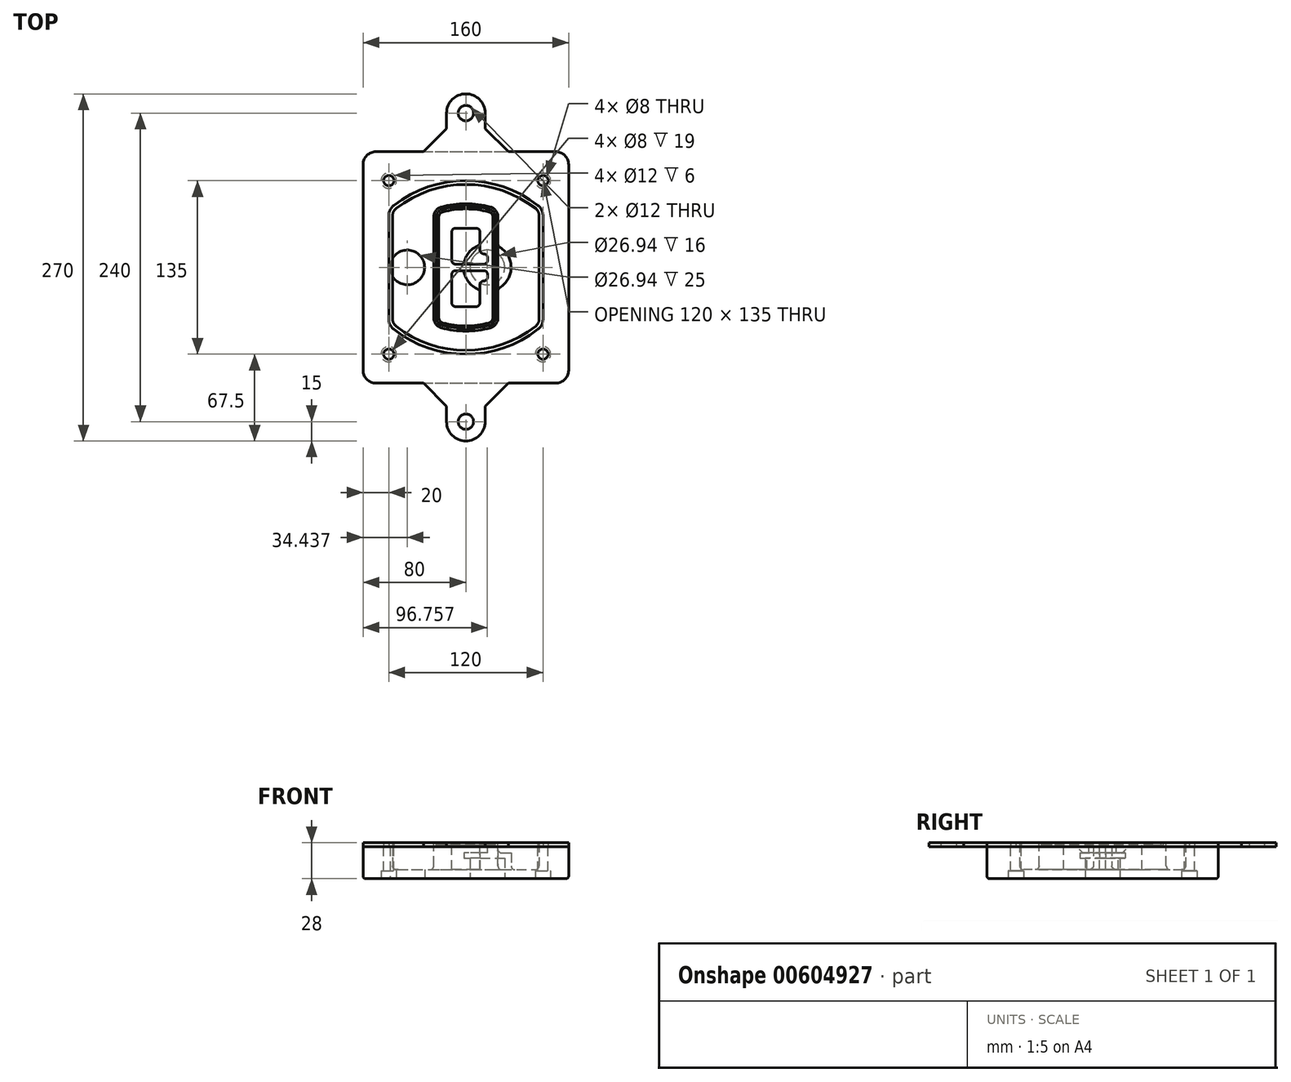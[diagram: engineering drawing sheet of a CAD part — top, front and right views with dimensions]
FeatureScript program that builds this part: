
annotation { "Feature Type Name" : "Feature", "Feature Type Description" : "" }
export const myFeature = defineFeature(function(context is Context, id is Id, definition is map)
    precondition{}
    {
        {
            var Q0;
            Q0=qCreatedBy(makeId("Top.planeOp"),FACE);
            var sketch = newSketch(context, id + "F0", { "sketchPlane" : qUnion([Q0])});
            skPoint(sketch, "E0.rect.middle", {"position": v(0, 0) * mm});
            skLineSegment(sketch, "E1.bottom", {"start": v(-70, -90) * mm, "end": v(70, -90) * mm});
            skLineSegment(sketch, "E1.top", {"start": v(-70, 90) * mm, "end": v(70, 90) * mm});
            skLineSegment(sketch, "E1.left", {"start": v(-80, -80) * mm, "end": v(-80, 80) * mm});
            skLineSegment(sketch, "E1.right", {"start": v(80, -80) * mm, "end": v(80, 80) * mm});
            skLineSegment(sketch, "E2", {"start": v(-80, 90) * mm, "end": v(80, -90) * mm, "construction": true});
            skLineSegment(sketch, "E3", {"start": v(80, 90) * mm, "end": v(-80, -90) * mm, "construction": true});
            skCircle(sketch, "E4", {"center": v(-60, 67.5) * mm, "radius": 4 * mm});
            skCircle(sketch, "E5", {"center": v(60, 67.5) * mm, "radius": 4 * mm});
            skCircle(sketch, "E6", {"center": v(60, -67.5) * mm, "radius": 4 * mm});
            skCircle(sketch, "E7", {"center": v(-60, -67.5) * mm, "radius": 4 * mm});
            skLineSegment(sketch, "E8", {"start": v(-60, 67.5) * mm, "end": v(60, 67.5) * mm, "construction": true});
            skLineSegment(sketch, "E9", {"start": v(60, 67.5) * mm, "end": v(60, -67.5) * mm, "construction": true});
            skLineSegment(sketch, "E10", {"start": v(60, -67.5) * mm, "end": v(-60, -67.5) * mm, "construction": true});
            skLineSegment(sketch, "E11", {"start": v(-60, -67.5) * mm, "end": v(-60, 67.5) * mm, "construction": true});
            skLineSegment(sketch, "E12", {"start": v(-60, 40.3) * mm, "end": v(-60, -40.3) * mm});
            skLineSegment(sketch, "E13", {"start": v(60, 40.3) * mm, "end": v(60, -40.3) * mm});
            skArc(sketch, "E14", {"start": v(56.15, 48.18) * mm, "mid": v(0, 67.5) * mm, "end": v(-56.15, 48.18) * mm});
            skArc(sketch, "E15", {"start": v(-56.15, -48.18) * mm, "mid": v(0, -67.5) * mm, "end": v(56.15, -48.18) * mm});
            skLineSegment(sketch, "E16", {"start": v(-60, 0) * mm, "end": v(60, 0) * mm, "construction": true});
            skPoint(sketch, "E17.visualSharp", {"position": v(-60, -45) * mm});
            skArc(sketch, "E17.filletArc", {"start": v(-60, -40.3) * mm, "mid": v(-58.99, -44.68) * mm, "end": v(-56.15, -48.18) * mm});
            skPoint(sketch, "E18.visualSharp", {"position": v(-60, 45) * mm});
            skArc(sketch, "E18.filletArc", {"start": v(-56.15, 48.18) * mm, "mid": v(-58.99, 44.68) * mm, "end": v(-60, 40.3) * mm});
            skPoint(sketch, "E19.visualSharp", {"position": v(60, 45) * mm});
            skArc(sketch, "E19.filletArc", {"start": v(60, 40.3) * mm, "mid": v(58.99, 44.68) * mm, "end": v(56.15, 48.18) * mm});
            skPoint(sketch, "E20.visualSharp", {"position": v(60, -45) * mm});
            skArc(sketch, "E20.filletArc", {"start": v(56.15, -48.18) * mm, "mid": v(58.99, -44.68) * mm, "end": v(60, -40.3) * mm});
            skPoint(sketch, "E21.visualSharp", {"position": v(-80, 90) * mm});
            skArc(sketch, "E21.filletArc", {"start": v(-70, 90) * mm, "mid": v(-77.07, 87.07) * mm, "end": v(-80, 80) * mm});
            skPoint(sketch, "E22.visualSharp", {"position": v(80, 90) * mm});
            skArc(sketch, "E22.filletArc", {"start": v(80, 80) * mm, "mid": v(77.07, 87.07) * mm, "end": v(70, 90) * mm});
            skPoint(sketch, "E23.visualSharp", {"position": v(80, -90) * mm});
            skArc(sketch, "E23.filletArc", {"start": v(70, -90) * mm, "mid": v(77.07, -87.07) * mm, "end": v(80, -80) * mm});
            skPoint(sketch, "E24.visualSharp", {"position": v(-80, -90) * mm});
            skArc(sketch, "E24.filletArc", {"start": v(-80, -80) * mm, "mid": v(-77.07, -87.07) * mm, "end": v(-70, -90) * mm});
            skArc(sketch, "E25.0", {"start": v(57, 40.3) * mm, "mid": v(56.3, 43.36) * mm, "end": v(54.3, 45.81) * mm});
            skLineSegment(sketch, "E25.1", {"start": v(57, 40.3) * mm, "end": v(57, -40.3) * mm});
            skArc(sketch, "E25.2", {"start": v(54.3, -45.81) * mm, "mid": v(56.3, -43.36) * mm, "end": v(57, -40.3) * mm});
            skArc(sketch, "E25.3", {"start": v(-54.3, -45.81) * mm, "mid": v(0, -64.5) * mm, "end": v(54.3, -45.81) * mm});
            skArc(sketch, "E25.4", {"start": v(-57, -40.3) * mm, "mid": v(-56.3, -43.36) * mm, "end": v(-54.3, -45.81) * mm});
            skArc(sketch, "E25.5", {"start": v(54.3, 45.81) * mm, "mid": v(0, 64.5) * mm, "end": v(-54.3, 45.81) * mm});
            skLineSegment(sketch, "E25.6", {"start": v(-57, 40.3) * mm, "end": v(-57, -40.3) * mm});
            skArc(sketch, "E25.7", {"start": v(-54.3, 45.81) * mm, "mid": v(-56.3, 43.36) * mm, "end": v(-57, 40.3) * mm});
            skArc(sketch, "E26.0", {"start": v(-58.62, 51.33) * mm, "mid": v(-62.58, 46.43) * mm, "end": v(-64, 40.3) * mm});
            skArc(sketch, "E26.1", {"start": v(58.62, 51.33) * mm, "mid": v(0, 71.5) * mm, "end": v(-58.62, 51.33) * mm});
            skArc(sketch, "E26.2", {"start": v(64, 40.3) * mm, "mid": v(62.58, 46.43) * mm, "end": v(58.62, 51.33) * mm});
            skLineSegment(sketch, "E26.3", {"start": v(64, 40.3) * mm, "end": v(64, -40.3) * mm});
            skArc(sketch, "E26.4", {"start": v(58.62, -51.33) * mm, "mid": v(62.58, -46.43) * mm, "end": v(64, -40.3) * mm});
            skLineSegment(sketch, "E26.5", {"start": v(-64, 40.3) * mm, "end": v(-64, -40.3) * mm});
            skArc(sketch, "E26.6", {"start": v(-58.62, -51.33) * mm, "mid": v(0, -71.5) * mm, "end": v(58.62, -51.33) * mm});
            skArc(sketch, "E26.7", {"start": v(-64, -40.3) * mm, "mid": v(-62.58, -46.43) * mm, "end": v(-58.62, -51.33) * mm});
            skSolve(sketch);
        }
        {
            var Q0;
            Q0=makeQuery(id+"F0.imprint","IMPRINT",FACE,{"disambiguationData":[TD([[makeQuery(id+"F0.imprint","IMPRINT",EDGE,{"derivedFrom":sQuery(id+"F0.wireOp",EDGE,"E1.bottom")}),1.0]])]});
            var Q1;
            Q1=makeQuery(id+"F0.imprint","IMPRINT",FACE,{"disambiguationData":[TD([[makeQuery(id+"F0.imprint","IMPRINT",EDGE,{"derivedFrom":sQuery(id+"F0.wireOp",EDGE,"E12")}),1.0]])]});
            var Q2;
            Q2=makeQuery(id+"F0.imprint","IMPRINT",FACE,{"disambiguationData":[TD([[makeQuery(id+"F0.imprint","IMPRINT",EDGE,{"derivedFrom":sQuery(id+"F0.wireOp",EDGE,"E25.0")}),1.0]])]});
            var Q3;
            Q3=makeQuery(id+"F0.imprint","IMPRINT",FACE,{"disambiguationData":[TD([[makeQuery(id+"F0.imprint","IMPRINT",EDGE,{"derivedFrom":sQuery(id+"F0.wireOp",EDGE,"E12")}),-1.0]])]});
            extrude(context, id + "F1", {"entities" : qUnion([Q0, Q1, Q2, Q3]), "oppositeDirection" : true, "depth" : 25 * mm});
        }
        {
            var Q0;
            Q0=makeQuery(id+"F0.imprint","IMPRINT",FACE,{"disambiguationData":[TD([[makeQuery(id+"F0.imprint","IMPRINT",EDGE,{"derivedFrom":sQuery(id+"F0.wireOp",EDGE,"E12")}),1.0]])]});
            extrude(context, id + "F2", {"entities" : qUnion([Q0]), "operationType" : NewBodyOperationType.ADD, "depth" : 3 * mm});
        }
        {
            var Q0;
            Q0=makeQuery(id+"F0.imprint","IMPRINT",FACE,{"disambiguationData":[TD([[makeQuery(id+"F0.imprint","IMPRINT",EDGE,{"derivedFrom":sQuery(id+"F0.wireOp",EDGE,"E25.0")}),1.0]])]});
            extrude(context, id + "F3", {"entities" : qUnion([Q0]), "operationType" : NewBodyOperationType.REMOVE, "oppositeDirection" : true, "depth" : 18 * mm});
        }
        {
            var Q0;
            Q0=makeQuery(id+"F2.opExtrude","CAP_FACE",FACE,{"disambiguationData":[OSD([sQuery(id+"F0.wireOp",EDGE,"E12"),sQuery(id+"F0.wireOp",EDGE,"E13"),sQuery(id+"F0.wireOp",EDGE,"E14"),sQuery(id+"F0.wireOp",EDGE,"E15"),sQuery(id+"F0.wireOp",EDGE,"E17.filletArc"),sQuery(id+"F0.wireOp",EDGE,"E18.filletArc"),sQuery(id+"F0.wireOp",EDGE,"E19.filletArc"),sQuery(id+"F0.wireOp",EDGE,"E20.filletArc"),sQuery(id+"F0.wireOp",EDGE,"E25.0"),sQuery(id+"F0.wireOp",EDGE,"E25.1"),sQuery(id+"F0.wireOp",EDGE,"E25.2"),sQuery(id+"F0.wireOp",EDGE,"E25.3"),sQuery(id+"F0.wireOp",EDGE,"E25.4"),sQuery(id+"F0.wireOp",EDGE,"E25.5"),sQuery(id+"F0.wireOp",EDGE,"E25.6"),sQuery(id+"F0.wireOp",EDGE,"E25.7")])],"isStart":false});
            var sketch = newSketch(context, id + "F4", { "sketchPlane" : qUnion([Q0])});
            skArc(sketch, "E27.0", {"start": v(-19.08, -46.97) * mm, "mid": v(0, -49.5) * mm, "end": v(19.08, -46.97) * mm});
            skArc(sketch, "E28.0", {"start": v(19.08, 46.97) * mm, "mid": v(0, 49.5) * mm, "end": v(-19.08, 46.97) * mm});
            skLineSegment(sketch, "E29", {"start": v(-25, 39.25) * mm, "end": v(-25, -39.25) * mm});
            skLineSegment(sketch, "E30", {"start": v(25, 39.25) * mm, "end": v(25, -39.25) * mm});
            skLineSegment(sketch, "E31", {"start": v(-25, 45.1) * mm, "end": v(25, 45.1) * mm, "construction": true});
            skLineSegment(sketch, "E32", {"start": v(-25, -45.1) * mm, "end": v(25, -45.1) * mm, "construction": true});
            skPoint(sketch, "E33.visualSharp", {"position": v(-25, 45.1) * mm});
            skArc(sketch, "E33.filletArc", {"start": v(-19.08, 46.97) * mm, "mid": v(-23.35, 44.11) * mm, "end": v(-25, 39.25) * mm});
            skPoint(sketch, "E34.visualSharp", {"position": v(25, 45.1) * mm});
            skArc(sketch, "E34.filletArc", {"start": v(25, 39.25) * mm, "mid": v(23.35, 44.11) * mm, "end": v(19.08, 46.97) * mm});
            skPoint(sketch, "E35.visualSharp", {"position": v(25, -45.1) * mm});
            skArc(sketch, "E35.filletArc", {"start": v(19.08, -46.97) * mm, "mid": v(23.35, -44.11) * mm, "end": v(25, -39.25) * mm});
            skPoint(sketch, "E36.visualSharp", {"position": v(-25, -45.1) * mm});
            skArc(sketch, "E36.filletArc", {"start": v(-25, -39.25) * mm, "mid": v(-23.35, -44.11) * mm, "end": v(-19.08, -46.97) * mm});
            skArc(sketch, "E37.0", {"start": v(54.3, 45.81) * mm, "mid": v(0, 64.5) * mm, "end": v(-54.3, 45.81) * mm});
            skArc(sketch, "E37.1", {"start": v(-54.3, 45.81) * mm, "mid": v(-56.3, 43.36) * mm, "end": v(-57, 40.3) * mm});
            skLineSegment(sketch, "E37.2", {"start": v(-57, 40.3) * mm, "end": v(-57, -40.3) * mm});
            skArc(sketch, "E37.3", {"start": v(-57, -40.3) * mm, "mid": v(-56.3, -43.36) * mm, "end": v(-54.3, -45.81) * mm});
            skArc(sketch, "E37.4", {"start": v(-54.3, -45.81) * mm, "mid": v(0, -64.5) * mm, "end": v(54.3, -45.81) * mm});
            skArc(sketch, "E37.5", {"start": v(54.3, -45.81) * mm, "mid": v(56.3, -43.36) * mm, "end": v(57, -40.3) * mm});
            skLineSegment(sketch, "E37.6", {"start": v(57, 40.3) * mm, "end": v(57, -40.3) * mm});
            skArc(sketch, "E37.7", {"start": v(57, 40.3) * mm, "mid": v(56.3, 43.36) * mm, "end": v(54.3, 45.81) * mm});
            skLineSegment(sketch, "E38.0", {"start": v(23, 39.25) * mm, "end": v(23, -39.25) * mm});
            skArc(sketch, "E38.1", {"start": v(18.56, -45.04) * mm, "mid": v(21.76, -42.9) * mm, "end": v(23, -39.25) * mm});
            skArc(sketch, "E38.2", {"start": v(-18.56, -45.04) * mm, "mid": v(0, -47.5) * mm, "end": v(18.56, -45.04) * mm});
            skArc(sketch, "E38.3", {"start": v(-23, -39.25) * mm, "mid": v(-21.76, -42.9) * mm, "end": v(-18.56, -45.04) * mm});
            skLineSegment(sketch, "E38.4", {"start": v(-23, 39.25) * mm, "end": v(-23, -39.25) * mm});
            skArc(sketch, "E38.5", {"start": v(23, 39.25) * mm, "mid": v(21.76, 42.9) * mm, "end": v(18.56, 45.04) * mm});
            skArc(sketch, "E38.6", {"start": v(-18.56, 45.04) * mm, "mid": v(-21.76, 42.9) * mm, "end": v(-23, 39.25) * mm});
            skArc(sketch, "E38.7", {"start": v(18.56, 45.04) * mm, "mid": v(0, 47.5) * mm, "end": v(-18.56, 45.04) * mm});
            skArc(sketch, "E39.0", {"start": v(21, 39.25) * mm, "mid": v(20.18, 41.68) * mm, "end": v(18.04, 43.1) * mm});
            skLineSegment(sketch, "E39.1", {"start": v(21, 39.25) * mm, "end": v(21, -39.25) * mm});
            skArc(sketch, "E39.2", {"start": v(18.04, -43.1) * mm, "mid": v(20.18, -41.68) * mm, "end": v(21, -39.25) * mm});
            skArc(sketch, "E39.3", {"start": v(-18.04, -43.1) * mm, "mid": v(0, -45.5) * mm, "end": v(18.04, -43.1) * mm});
            skArc(sketch, "E39.4", {"start": v(-21, -39.25) * mm, "mid": v(-20.18, -41.68) * mm, "end": v(-18.04, -43.1) * mm});
            skArc(sketch, "E39.5", {"start": v(18.04, 43.1) * mm, "mid": v(0, 45.5) * mm, "end": v(-18.04, 43.1) * mm});
            skLineSegment(sketch, "E39.6", {"start": v(-21, 39.25) * mm, "end": v(-21, -39.25) * mm});
            skArc(sketch, "E39.7", {"start": v(-18.04, 43.1) * mm, "mid": v(-20.18, 41.68) * mm, "end": v(-21, 39.25) * mm});
            skLineSegment(sketch, "E40", {"start": v(-25, 0) * mm, "end": v(25, 0) * mm, "construction": true});
            skLineSegment(sketch, "E41", {"start": v(-11, 5.5) * mm, "end": v(-11, 27.5) * mm});
            skLineSegment(sketch, "E42", {"start": v(-8, 30.5) * mm, "end": v(8, 30.5) * mm});
            skLineSegment(sketch, "E43", {"start": v(11, 27.5) * mm, "end": v(11, 13.5) * mm});
            skLineSegment(sketch, "E44", {"start": v(14, 10.5) * mm, "end": v(14, 10.5) * mm});
            skLineSegment(sketch, "E45", {"start": v(17, 7.5) * mm, "end": v(17, 5.5) * mm});
            skLineSegment(sketch, "E46", {"start": v(14, 2.5) * mm, "end": v(-8, 2.5) * mm});
            skPoint(sketch, "E47.visualSharp", {"position": v(-11, 30.5) * mm});
            skArc(sketch, "E47.filletArc", {"start": v(-8, 30.5) * mm, "mid": v(-10.12, 29.62) * mm, "end": v(-11, 27.5) * mm});
            skPoint(sketch, "E48.visualSharp", {"position": v(11, 30.5) * mm});
            skArc(sketch, "E48.filletArc", {"start": v(11, 27.5) * mm, "mid": v(10.12, 29.62) * mm, "end": v(8, 30.5) * mm});
            skPoint(sketch, "E49.visualSharp", {"position": v(11, 10.5) * mm});
            skArc(sketch, "E49.filletArc", {"start": v(11, 13.5) * mm, "mid": v(11.88, 11.38) * mm, "end": v(14, 10.5) * mm});
            skPoint(sketch, "E50.visualSharp", {"position": v(17, 10.5) * mm});
            skArc(sketch, "E50.filletArc", {"start": v(17, 7.5) * mm, "mid": v(16.12, 9.62) * mm, "end": v(14, 10.5) * mm});
            skPoint(sketch, "E51.visualSharp", {"position": v(17, 2.5) * mm});
            skArc(sketch, "E51.filletArc", {"start": v(14, 2.5) * mm, "mid": v(16.12, 3.38) * mm, "end": v(17, 5.5) * mm});
            skPoint(sketch, "E52.visualSharp", {"position": v(-11, 2.5) * mm});
            skArc(sketch, "E52.filletArc", {"start": v(-11, 5.5) * mm, "mid": v(-10.12, 3.38) * mm, "end": v(-8, 2.5) * mm});
            skLineSegment(sketch, "E53.0.MirrorCS", {"start": v(14, -2.5) * mm, "end": v(-8, -2.5) * mm});
            skArc(sketch, "E54.0.MirrorCS", {"start": v(-11, -5.5) * mm, "mid": v(-10.12, -3.38) * mm, "end": v(-8, -2.5) * mm});
            skLineSegment(sketch, "E55.0.MirrorCS", {"start": v(-11, -5.5) * mm, "end": v(-11, -27.5) * mm});
            skArc(sketch, "E56.0.MirrorCS", {"start": v(-8, -30.5) * mm, "mid": v(-10.12, -29.62) * mm, "end": v(-11, -27.5) * mm});
            skLineSegment(sketch, "E57.0.MirrorCS", {"start": v(-8, -30.5) * mm, "end": v(8, -30.5) * mm});
            skArc(sketch, "E58.0.MirrorCS", {"start": v(11, -27.5) * mm, "mid": v(10.12, -29.62) * mm, "end": v(8, -30.5) * mm});
            skLineSegment(sketch, "E59.0.MirrorCS", {"start": v(11, -27.5) * mm, "end": v(11, -13.5) * mm});
            skArc(sketch, "E60.0.MirrorCS", {"start": v(11, -13.5) * mm, "mid": v(11.88, -11.38) * mm, "end": v(14, -10.5) * mm});
            skArc(sketch, "E61.0.MirrorCS", {"start": v(17, -7.5) * mm, "mid": v(16.12, -9.62) * mm, "end": v(14, -10.5) * mm});
            skLineSegment(sketch, "E62.0.MirrorCS", {"start": v(17, -7.5) * mm, "end": v(17, -5.5) * mm});
            skArc(sketch, "E63.0.MirrorCS", {"start": v(14, -2.5) * mm, "mid": v(16.12, -3.38) * mm, "end": v(17, -5.5) * mm});
            skSolve(sketch);
        }
        {
            var Q0;
            Q0=makeQuery(id+"F4.imprint","IMPRINT",FACE,{"disambiguationData":[TD([[makeQuery(id+"F4.imprint","IMPRINT",EDGE,{"derivedFrom":sQuery(id+"F4.wireOp",EDGE,"E27.0")}),1.0]])]});
            var Q1;
            Q1=makeQuery(id+"F4.imprint","IMPRINT",FACE,{"disambiguationData":[TD([[makeQuery(id+"F4.imprint","IMPRINT",EDGE,{"derivedFrom":sQuery(id+"F4.wireOp",EDGE,"E38.0")}),-1.0]])]});
            var Q2;
            Q2=makeQuery(id+"F4.imprint","IMPRINT",FACE,{"disambiguationData":[TD([[makeQuery(id+"F4.imprint","IMPRINT",EDGE,{"derivedFrom":sQuery(id+"F4.wireOp",EDGE,"E39.0")}),1.0]])]});
            extrude(context, id + "F5", {"entities" : qUnion([Q0, Q1, Q2]), "operationType" : NewBodyOperationType.ADD, "endBound" : BoundingType.UP_TO_NEXT, "oppositeDirection" : true, "depth" : 25 * mm});
        }
        {
            var Q0;
            Q0=makeQuery(id+"F4.imprint","IMPRINT",FACE,{"disambiguationData":[TD([[makeQuery(id+"F4.imprint","IMPRINT",EDGE,{"derivedFrom":sQuery(id+"F4.wireOp",EDGE,"E38.0")}),-1.0]])]});
            extrude(context, id + "F6", {"entities" : qUnion([Q0]), "operationType" : NewBodyOperationType.REMOVE, "oppositeDirection" : true, "depth" : 2 * mm});
        }
        {
            var Q0;
            Q0=makeQuery(id+"F1.opExtrude","CAP_FACE",FACE,{"disambiguationData":[OSD([sQuery(id+"F0.wireOp",EDGE,"E1.bottom"),sQuery(id+"F0.wireOp",EDGE,"E1.top"),sQuery(id+"F0.wireOp",EDGE,"E1.left"),sQuery(id+"F0.wireOp",EDGE,"E1.right"),sQuery(id+"F0.wireOp",EDGE,"E4"),sQuery(id+"F0.wireOp",EDGE,"E5"),sQuery(id+"F0.wireOp",EDGE,"E6"),sQuery(id+"F0.wireOp",EDGE,"E7"),sQuery(id+"F0.wireOp",EDGE,"E21.filletArc"),sQuery(id+"F0.wireOp",EDGE,"E22.filletArc"),sQuery(id+"F0.wireOp",EDGE,"E23.filletArc"),sQuery(id+"F0.wireOp",EDGE,"E24.filletArc")])],"isStart":false});
            var sketch = newSketch(context, id + "F7", { "sketchPlane" : qUnion([Q0])});
            skCircle(sketch, "E64", {"center": v(16.76, 0) * mm, "radius": 13.47 * mm});
            skCircle(sketch, "E65", {"center": v(-45.56, 0) * mm, "radius": 13.47 * mm});
            skLineSegment(sketch, "E66", {"start": v(80, 0) * mm, "end": v(-80, 0) * mm});
            skCircle(sketch, "E67", {"center": v(16.76, 0) * mm, "radius": 18.47 * mm});
            skCircle(sketch, "E68", {"center": v(60, -67.5) * mm, "radius": 6 * mm});
            skCircle(sketch, "E69", {"center": v(-60, -67.5) * mm, "radius": 6 * mm});
            skCircle(sketch, "E70", {"center": v(-60, 67.5) * mm, "radius": 6 * mm});
            skCircle(sketch, "E71", {"center": v(60, 67.5) * mm, "radius": 6 * mm});
            skSolve(sketch);
        }
        {
            var Q0;
            {var subQ1=sQuery(id+"F7.wireOp",EDGE,"E66");var subQ4=sQuery(id+"F7.wireOp",EDGE,"E64");var subQ6=makeQuery(id+"F7.imprint","INTERSECT",VERTEX,{"disambiguationData":[OD(0.0)],"derivedFrom":[subQ4,subQ1]});Q0=makeQuery(id+"F7.imprint","IMPRINT",FACE,{"disambiguationData":[TD([[makeQuery(id+"F7.imprint","IMPRINT",EDGE,{"disambiguationData":[TD([[subQ6,-1.0]])],"derivedFrom":subQ4}),-1.0]])]});}
            var Q1;
            {var subQ0=sQuery(id+"F7.wireOp",EDGE,"E66");var subQ1=sQuery(id+"F7.wireOp",EDGE,"E64");var subQ3=makeQuery(id+"F7.imprint","INTERSECT",VERTEX,{"disambiguationData":[OD(0.0)],"derivedFrom":[subQ1,subQ0]});Q1=makeQuery(id+"F7.imprint","IMPRINT",FACE,{"disambiguationData":[TD([[makeQuery(id+"F7.imprint","IMPRINT",EDGE,{"disambiguationData":[TD([[subQ3,-1.0]])],"derivedFrom":subQ1}),1.0]])]});}
            var Q2;
            {var subQ0=sQuery(id+"F7.wireOp",EDGE,"E66");var subQ1=sQuery(id+"F7.wireOp",EDGE,"E64");var subQ3=makeQuery(id+"F7.imprint","INTERSECT",VERTEX,{"disambiguationData":[OD(0.0)],"derivedFrom":[subQ1,subQ0]});Q2=makeQuery(id+"F7.imprint","IMPRINT",FACE,{"disambiguationData":[TD([[makeQuery(id+"F7.imprint","IMPRINT",EDGE,{"disambiguationData":[TD([[subQ3,1.0]])],"derivedFrom":subQ1}),1.0]])]});}
            var Q3;
            {var subQ1=sQuery(id+"F7.wireOp",EDGE,"E66");var subQ4=sQuery(id+"F7.wireOp",EDGE,"E64");var subQ6=makeQuery(id+"F7.imprint","INTERSECT",VERTEX,{"disambiguationData":[OD(0.0)],"derivedFrom":[subQ4,subQ1]});Q3=makeQuery(id+"F7.imprint","IMPRINT",FACE,{"disambiguationData":[TD([[makeQuery(id+"F7.imprint","IMPRINT",EDGE,{"disambiguationData":[TD([[subQ6,1.0]])],"derivedFrom":subQ4}),-1.0]])]});}
            extrude(context, id + "F8", {"entities" : qUnion([Q0, Q1, Q2, Q3]), "operationType" : NewBodyOperationType.ADD, "oppositeDirection" : true, "depth" : 20 * mm});
        }
        {
            var Q0;
            {var subQ0=sQuery(id+"F7.wireOp",EDGE,"E66");var subQ1=sQuery(id+"F7.wireOp",EDGE,"E64");var subQ3=makeQuery(id+"F7.imprint","INTERSECT",VERTEX,{"disambiguationData":[OD(0.0)],"derivedFrom":[subQ1,subQ0]});Q0=makeQuery(id+"F7.imprint","IMPRINT",FACE,{"disambiguationData":[TD([[makeQuery(id+"F7.imprint","IMPRINT",EDGE,{"disambiguationData":[TD([[subQ3,-1.0]])],"derivedFrom":subQ1}),1.0]])]});}
            var Q1;
            {var subQ0=sQuery(id+"F7.wireOp",EDGE,"E66");var subQ1=sQuery(id+"F7.wireOp",EDGE,"E64");var subQ3=makeQuery(id+"F7.imprint","INTERSECT",VERTEX,{"disambiguationData":[OD(0.0)],"derivedFrom":[subQ1,subQ0]});Q1=makeQuery(id+"F7.imprint","IMPRINT",FACE,{"disambiguationData":[TD([[makeQuery(id+"F7.imprint","IMPRINT",EDGE,{"disambiguationData":[TD([[subQ3,1.0]])],"derivedFrom":subQ1}),1.0]])]});}
            extrude(context, id + "F9", {"entities" : qUnion([Q0, Q1]), "operationType" : NewBodyOperationType.REMOVE, "oppositeDirection" : true, "depth" : 16 * mm});
        }
        {
            var Q0;
            {var subQ0=sQuery(id+"F7.wireOp",EDGE,"E66");var subQ1=sQuery(id+"F7.wireOp",EDGE,"E65");var subQ3=makeQuery(id+"F7.imprint","INTERSECT",VERTEX,{"disambiguationData":[OD(0.0)],"derivedFrom":[subQ1,subQ0]});Q0=makeQuery(id+"F7.imprint","IMPRINT",FACE,{"disambiguationData":[TD([[makeQuery(id+"F7.imprint","IMPRINT",EDGE,{"disambiguationData":[TD([[subQ3,-1.0]])],"derivedFrom":subQ1}),1.0]])]});}
            var Q1;
            {var subQ0=sQuery(id+"F7.wireOp",EDGE,"E66");var subQ1=sQuery(id+"F7.wireOp",EDGE,"E65");var subQ3=makeQuery(id+"F7.imprint","INTERSECT",VERTEX,{"disambiguationData":[OD(0.0)],"derivedFrom":[subQ1,subQ0]});Q1=makeQuery(id+"F7.imprint","IMPRINT",FACE,{"disambiguationData":[TD([[makeQuery(id+"F7.imprint","IMPRINT",EDGE,{"disambiguationData":[TD([[subQ3,1.0]])],"derivedFrom":subQ1}),1.0]])]});}
            extrude(context, id + "F10", {"entities" : qUnion([Q0, Q1]), "operationType" : NewBodyOperationType.REMOVE, "oppositeDirection" : true, "depth" : 25 * mm});
        }
        {
            var Q0;
            Q0=makeQuery(id+"F7.imprint","IMPRINT",FACE,{"disambiguationData":[TD([[makeQuery(id+"F7.imprint","IMPRINT",EDGE,{"derivedFrom":sQuery(id+"F7.wireOp",EDGE,"E68")}),1.0]])]});
            var Q1;
            Q1=makeQuery(id+"F7.imprint","IMPRINT",FACE,{"disambiguationData":[TD([[makeQuery(id+"F7.imprint","IMPRINT",EDGE,{"derivedFrom":makeQuery(id+"F1.opExtrude","CAP_EDGE",EDGE,{"disambiguationData":[OSD([sQuery(id+"F0.wireOp",EDGE,"E5")])],"isStart":false})}),-1.0]])]});
            var Q2;
            Q2=makeQuery(id+"F7.imprint","IMPRINT",FACE,{"disambiguationData":[TD([[makeQuery(id+"F7.imprint","IMPRINT",EDGE,{"derivedFrom":sQuery(id+"F7.wireOp",EDGE,"E69")}),1.0]])]});
            var Q3;
            Q3=makeQuery(id+"F7.imprint","IMPRINT",FACE,{"disambiguationData":[TD([[makeQuery(id+"F7.imprint","IMPRINT",EDGE,{"derivedFrom":makeQuery(id+"F1.opExtrude","CAP_EDGE",EDGE,{"disambiguationData":[OSD([sQuery(id+"F0.wireOp",EDGE,"E4")])],"isStart":false})}),-1.0]])]});
            var Q4;
            Q4=makeQuery(id+"F7.imprint","IMPRINT",FACE,{"disambiguationData":[TD([[makeQuery(id+"F7.imprint","IMPRINT",EDGE,{"derivedFrom":sQuery(id+"F7.wireOp",EDGE,"E70")}),1.0]])]});
            var Q5;
            Q5=makeQuery(id+"F7.imprint","IMPRINT",FACE,{"disambiguationData":[TD([[makeQuery(id+"F7.imprint","IMPRINT",EDGE,{"derivedFrom":makeQuery(id+"F1.opExtrude","CAP_EDGE",EDGE,{"disambiguationData":[OSD([sQuery(id+"F0.wireOp",EDGE,"E7")])],"isStart":false})}),-1.0]])]});
            var Q6;
            Q6=makeQuery(id+"F7.imprint","IMPRINT",FACE,{"disambiguationData":[TD([[makeQuery(id+"F7.imprint","IMPRINT",EDGE,{"derivedFrom":sQuery(id+"F7.wireOp",EDGE,"E71")}),1.0]])]});
            var Q7;
            Q7=makeQuery(id+"F7.imprint","IMPRINT",FACE,{"disambiguationData":[TD([[makeQuery(id+"F7.imprint","IMPRINT",EDGE,{"derivedFrom":makeQuery(id+"F1.opExtrude","CAP_EDGE",EDGE,{"disambiguationData":[OSD([sQuery(id+"F0.wireOp",EDGE,"E6")])],"isStart":false})}),-1.0]])]});
            extrude(context, id + "F11", {"entities" : qUnion([Q0, Q1, Q2, Q3, Q4, Q5, Q6, Q7]), "operationType" : NewBodyOperationType.REMOVE, "oppositeDirection" : true, "depth" : 6 * mm});
        }
        {
            var Q0;
            Q0=makeQuery(id+"F9.boolean.opBoolean","COPY",FACE,{"derivedFrom":makeQuery(id+"F9.opExtrude","CAP_FACE",FACE,{"disambiguationData":[OSD([sQuery(id+"F7.wireOp",EDGE,"E64")])],"isStart":false})});
            var sketch = newSketch(context, id + "F12", { "sketchPlane" : qUnion([Q0])});
            skArc(sketch, "E72.0", {"start": v(11, 17.55) * mm, "mid": v(2.57, 11.82) * mm, "end": v(-1.54, 2.5) * mm});
            skArc(sketch, "E72.1", {"start": v(-1.54, -2.5) * mm, "mid": v(2.57, -11.82) * mm, "end": v(11, -17.55) * mm});
            skLineSegment(sketch, "E73", {"start": v(-1.54, -2.5) * mm, "end": v(14, -2.5) * mm});
            skLineSegment(sketch, "E74.0", {"start": v(14, 2.5) * mm, "end": v(-1.54, 2.5) * mm});
            skArc(sketch, "E74.1", {"start": v(14, 2.5) * mm, "mid": v(16.12, 3.38) * mm, "end": v(17, 5.5) * mm});
            skLineSegment(sketch, "E74.2", {"start": v(17, 7.5) * mm, "end": v(17, 5.5) * mm});
            skArc(sketch, "E74.3", {"start": v(17, 7.5) * mm, "mid": v(16.12, 9.62) * mm, "end": v(14, 10.5) * mm});
            skArc(sketch, "E74.4", {"start": v(11, 13.5) * mm, "mid": v(11.88, 11.38) * mm, "end": v(14, 10.5) * mm});
            skLineSegment(sketch, "E74.5", {"start": v(11, 17.55) * mm, "end": v(11, 13.5) * mm});
            skLineSegment(sketch, "E74.7", {"start": v(14, -2.5) * mm, "end": v(-1.54, -2.5) * mm});
            skArc(sketch, "E74.8", {"start": v(14, -2.5) * mm, "mid": v(16.12, -3.38) * mm, "end": v(17, -5.5) * mm});
            skLineSegment(sketch, "E74.9", {"start": v(17, -7.5) * mm, "end": v(17, -5.5) * mm});
            skArc(sketch, "E74.10", {"start": v(17, -7.5) * mm, "mid": v(16.12, -9.62) * mm, "end": v(14, -10.5) * mm});
            skArc(sketch, "E74.11", {"start": v(11, -13.5) * mm, "mid": v(11.88, -11.38) * mm, "end": v(14, -10.5) * mm});
            skLineSegment(sketch, "E74.12", {"start": v(11, -17.55) * mm, "end": v(11, -13.5) * mm});
            skPoint(sketch, "E75.orphan", {"position": v(11, -27.5) * mm});
            skPoint(sketch, "E76.orphan", {"position": v(-8, -2.5) * mm});
            skPoint(sketch, "E77.orphan", {"position": v(-8, 2.5) * mm});
            skPoint(sketch, "E78.orphan", {"position": v(11, 27.5) * mm});
            skSolve(sketch);
        }
        {
            var Q0;
            {var subQ7=sQuery(id+"F12.wireOp",EDGE,"E72.0");var subQ14=sQuery(id+"F12.wireOp",EDGE,"E72.1");var subQ16=sQuery(id+"F12.wireOp",EDGE,"E74.1");var subQ18=sQuery(id+"F12.wireOp",EDGE,"E74.8");Q0=qUnion([makeQuery(id+"F12.imprint","IMPRINT",FACE,{"disambiguationData":[TD([[makeQuery(id+"F12.imprint","IMPRINT",EDGE,{"derivedFrom":subQ7}),1.0]])]}),makeQuery(id+"F12.imprint","IMPRINT",FACE,{"disambiguationData":[TD([[makeQuery(id+"F12.imprint","IMPRINT",EDGE,{"derivedFrom":subQ14}),1.0]])]}),makeQuery(id+"F12.imprint","IMPRINT",FACE,{"disambiguationData":[TD([[makeQuery(id+"F12.imprint","IMPRINT",EDGE,{"derivedFrom":subQ16}),1.0]])]}),makeQuery(id+"F12.imprint","IMPRINT",FACE,{"disambiguationData":[TD([[makeQuery(id+"F12.imprint","IMPRINT",EDGE,{"derivedFrom":subQ18}),-1.0]])]})]);}
            var Q1;
            Q1=makeQuery(id+"F5.boolean.opBoolean","SPLIT",FACE,{"disambiguationData":[TD([makeQuery(id+"F5.opExtrude","SWEPT_FACE",FACE,{"disambiguationData":[OSD([sQuery(id+"F4.wireOp",EDGE,"E41")])]})])],"derivedFrom":makeQuery(id+"F3.boolean.opBoolean","COPY",FACE,{"derivedFrom":makeQuery(id+"F3.opExtrude","CAP_FACE",FACE,{"disambiguationData":[OSD([sQuery(id+"F0.wireOp",EDGE,"E25.0"),sQuery(id+"F0.wireOp",EDGE,"E25.1"),sQuery(id+"F0.wireOp",EDGE,"E25.2"),sQuery(id+"F0.wireOp",EDGE,"E25.3"),sQuery(id+"F0.wireOp",EDGE,"E25.4"),sQuery(id+"F0.wireOp",EDGE,"E25.5"),sQuery(id+"F0.wireOp",EDGE,"E25.6"),sQuery(id+"F0.wireOp",EDGE,"E25.7")])],"isStart":false})})});
            extrude(context, id + "F13", {"entities" : qUnion([Q0]), "operationType" : NewBodyOperationType.REMOVE, "endBound" : BoundingType.UP_TO_SURFACE, "endBoundEntityFace" : qUnion([Q1]), "depth" : 25 * mm});
        }
        {
            var Q0;
            Q0=makeQuery(id+"F3.boolean.opBoolean","COPY",EDGE,{"derivedFrom":makeQuery(id+"F3.opExtrude","CAP_EDGE",EDGE,{"disambiguationData":[OSD([sQuery(id+"F0.wireOp",EDGE,"E25.6")])],"isStart":false})});
            var Q1;
            Q1=makeQuery(id+"F8.boolean.opBoolean","INTERSECT",EDGE,{"derivedFrom":[makeQuery(id+"F5.opExtrude","SWEPT_FACE",FACE,{"disambiguationData":[OSD([sQuery(id+"F4.wireOp",EDGE,"E30")])]}),makeQuery(id+"F8.opExtrude","CAP_FACE",FACE,{"disambiguationData":[OSD([sQuery(id+"F7.wireOp",EDGE,"E67")])],"isStart":false})]});
            var Q2;
            Q2=makeQuery(id+"F8.boolean.opBoolean","INTERSECT",EDGE,{"disambiguationData":[OD(1.0)],"derivedFrom":[makeQuery(id+"F5.opExtrude","SWEPT_FACE",FACE,{"disambiguationData":[OSD([sQuery(id+"F4.wireOp",EDGE,"E30")])]}),makeQuery(id+"F8.opExtrude","SWEPT_FACE",FACE,{"disambiguationData":[OSD([sQuery(id+"F7.wireOp",EDGE,"E67")])]})]});
            var Q3;
            {var subQ0=sQuery(id+"F4.wireOp",EDGE,"E30");Q3=makeQuery(id+"F8.boolean.opBoolean","SPLIT",EDGE,{"disambiguationData":[TD([makeQuery(id+"F5.opExtrude","SWEPT_FACE",FACE,{"disambiguationData":[OSD([sQuery(id+"F4.wireOp",EDGE,"E35.filletArc")])]})])],"derivedFrom":makeQuery(id+"F5.opExtrude","CAP_EDGE",EDGE,{"disambiguationData":[OSD([subQ0])],"isStart":false})});}
            var Q4;
            {var subQ0=sQuery(id+"F0.wireOp",EDGE,"E25.7");var subQ1=sQuery(id+"F0.wireOp",EDGE,"E25.1");var subQ2=sQuery(id+"F0.wireOp",EDGE,"E25.6");var subQ3=sQuery(id+"F0.wireOp",EDGE,"E25.5");var subQ4=sQuery(id+"F0.wireOp",EDGE,"E25.4");var subQ5=sQuery(id+"F0.wireOp",EDGE,"E25.0");var subQ6=sQuery(id+"F0.wireOp",EDGE,"E25.2");var subQ7=sQuery(id+"F0.wireOp",EDGE,"E25.3");Q4=makeQuery(id+"F8.boolean.opBoolean","INTERSECT",EDGE,{"derivedFrom":[makeQuery(id+"F5.boolean.opBoolean","SPLIT",FACE,{"disambiguationData":[TD([makeQuery(id+"F2.opExtrude","SWEPT_FACE",FACE,{"disambiguationData":[OSD([subQ5])]})])],"derivedFrom":makeQuery(id+"F3.boolean.opBoolean","COPY",FACE,{"derivedFrom":makeQuery(id+"F3.opExtrude","CAP_FACE",FACE,{"disambiguationData":[OSD([subQ5,subQ1,subQ6,subQ7,subQ4,subQ3,subQ2,subQ0])],"isStart":false})})}),makeQuery(id+"F8.opExtrude","SWEPT_FACE",FACE,{"disambiguationData":[OSD([sQuery(id+"F7.wireOp",EDGE,"E67")])]})]});}
            var Q5;
            Q5=makeQuery(id+"F8.boolean.opBoolean","INTERSECT",EDGE,{"disambiguationData":[OD(0.0)],"derivedFrom":[makeQuery(id+"F5.opExtrude","SWEPT_FACE",FACE,{"disambiguationData":[OSD([sQuery(id+"F4.wireOp",EDGE,"E30")])]}),makeQuery(id+"F8.opExtrude","SWEPT_FACE",FACE,{"disambiguationData":[OSD([sQuery(id+"F7.wireOp",EDGE,"E67")])]})]});
            fillet(context, id + "F14", {"entities" : qUnion([Q0, Q1, Q2, Q3, Q4, Q5]), "radius" : 3 * mm, "tangentPropagation" : true, "allowEdgeOverflow" : false});
        }
        {
            var Q0;
            Q0=makeQuery(id+"F1.opExtrude","CAP_EDGE",EDGE,{"disambiguationData":[OSD([sQuery(id+"F0.wireOp",EDGE,"E1.bottom")])],"isStart":false});
            fillet(context, id + "F15", {"entities" : qUnion([Q0]), "radius" : 2 * mm, "tangentPropagation" : true, "allowEdgeOverflow" : false});
        }
        {
            var Q0;
            {var subQ0=sQuery(id+"F0.wireOp",EDGE,"E21.filletArc");var subQ1=sQuery(id+"F0.wireOp",EDGE,"E7");var subQ2=sQuery(id+"F0.wireOp",EDGE,"E6");var subQ3=sQuery(id+"F0.wireOp",EDGE,"E5");var subQ4=sQuery(id+"F0.wireOp",EDGE,"E4");var subQ5=sQuery(id+"F0.wireOp",EDGE,"E22.filletArc");var subQ6=sQuery(id+"F0.wireOp",EDGE,"E1.bottom");var subQ7=sQuery(id+"F0.wireOp",EDGE,"E1.right");var subQ8=sQuery(id+"F0.wireOp",EDGE,"E1.top");var subQ9=sQuery(id+"F0.wireOp",EDGE,"E1.left");var subQ10=sQuery(id+"F0.wireOp",EDGE,"E23.filletArc");var subQ11=sQuery(id+"F0.wireOp",EDGE,"E24.filletArc");Q0=makeQuery(id+"F2.boolean.opBoolean","SPLIT",FACE,{"disambiguationData":[TD([makeQuery(id+"F1.opExtrude","SWEPT_FACE",FACE,{"disambiguationData":[OSD([subQ6])]})])],"derivedFrom":makeQuery(id+"F1.opExtrude","CAP_FACE",FACE,{"disambiguationData":[OSD([subQ6,subQ8,subQ9,subQ7,subQ4,subQ3,subQ2,subQ1,subQ0,subQ5,subQ10,subQ11])],"isStart":true})});}
            var sketch = newSketch(context, id + "F16", { "sketchPlane" : qUnion([Q0])});
            skLineSegment(sketch, "E79.0", {"start": v(-70, 90) * mm, "end": v(70, 90) * mm});
            skArc(sketch, "E80.0", {"start": v(-70, 90) * mm, "mid": v(-77.07, 87.07) * mm, "end": v(-80, 80) * mm});
            skLineSegment(sketch, "E81.0", {"start": v(-80, -80) * mm, "end": v(-80, 80) * mm});
            skArc(sketch, "E82.0", {"start": v(-80, -80) * mm, "mid": v(-77.07, -87.07) * mm, "end": v(-70, -90) * mm});
            skLineSegment(sketch, "E83.0", {"start": v(-70, -90) * mm, "end": v(70, -90) * mm});
            skArc(sketch, "E84.0", {"start": v(70, -90) * mm, "mid": v(77.07, -87.07) * mm, "end": v(80, -80) * mm});
            skLineSegment(sketch, "E85.0.0", {"start": v(70, 90) * mm, "end": v(-70, 90) * mm});
            skLineSegment(sketch, "E85.0.2", {"start": v(-80, 80) * mm, "end": v(-80, -80) * mm});
            skLineSegment(sketch, "E85.0.6", {"start": v(80, -80) * mm, "end": v(80, 80) * mm});
            skArc(sketch, "E85.0.7", {"start": v(80, 80) * mm, "mid": v(77.07, 87.07) * mm, "end": v(70, 90) * mm});
            skLineSegment(sketch, "E86.0", {"start": v(60, 40.3) * mm, "end": v(60, -40.3) * mm});
            skArc(sketch, "E87.0", {"start": v(56.15, 48.18) * mm, "mid": v(0, 67.5) * mm, "end": v(-56.15, 48.18) * mm});
            skLineSegment(sketch, "E88.0", {"start": v(-60, 40.3) * mm, "end": v(-60, -40.3) * mm});
            skLineSegment(sketch, "E89.0.0", {"start": v(60, -40.3) * mm, "end": v(60, 40.3) * mm});
            skArc(sketch, "E89.0.1", {"start": v(60, 40.3) * mm, "mid": v(58.99, 44.68) * mm, "end": v(56.15, 48.18) * mm});
            skArc(sketch, "E89.0.3", {"start": v(-56.15, 48.18) * mm, "mid": v(-58.99, 44.68) * mm, "end": v(-60, 40.3) * mm});
            skArc(sketch, "E89.0.5", {"start": v(-60, -40.3) * mm, "mid": v(-58.99, -44.68) * mm, "end": v(-56.15, -48.18) * mm});
            skArc(sketch, "E89.0.6", {"start": v(-56.15, -48.18) * mm, "mid": v(0, -67.5) * mm, "end": v(56.15, -48.18) * mm});
            skArc(sketch, "E89.0.7", {"start": v(56.15, -48.18) * mm, "mid": v(58.99, -44.68) * mm, "end": v(60, -40.3) * mm});
            skCircle(sketch, "E90.0", {"center": v(-60, 67.5) * mm, "radius": 4 * mm});
            skCircle(sketch, "E91.0", {"center": v(60, 67.5) * mm, "radius": 4 * mm});
            skCircle(sketch, "E92.0", {"center": v(60, -67.5) * mm, "radius": 4 * mm});
            skCircle(sketch, "E93.0", {"center": v(-60, -67.5) * mm, "radius": 4 * mm});
            skLineSegment(sketch, "E94", {"start": v(0, 90) * mm, "end": v(0, 120) * mm, "construction": true});
            skCircle(sketch, "E95", {"center": v(0, 120) * mm, "radius": 6 * mm});
            skArc(sketch, "E96", {"start": v(15, 120) * mm, "mid": v(0, 135) * mm, "end": v(-15, 120) * mm});
            skLineSegment(sketch, "E97", {"start": v(-15, 120) * mm, "end": v(-15, 108) * mm});
            skLineSegment(sketch, "E98", {"start": v(-15, 108) * mm, "end": v(-33, 90) * mm});
            skLineSegment(sketch, "E99", {"start": v(15, 120) * mm, "end": v(15, 108) * mm});
            skLineSegment(sketch, "E100", {"start": v(15, 108) * mm, "end": v(33, 90) * mm});
            skLineSegment(sketch, "E101", {"start": v(-80, 0) * mm, "end": v(80, 0) * mm, "construction": true});
            skLineSegment(sketch, "E102.MirrorCS", {"start": v(15, -120) * mm, "end": v(15, -108) * mm});
            skLineSegment(sketch, "E103.MirrorCS", {"start": v(15, -108) * mm, "end": v(33, -90) * mm});
            skArc(sketch, "E104.MirrorCS", {"start": v(15, -120) * mm, "mid": v(0, -135) * mm, "end": v(-15, -120) * mm});
            skLineSegment(sketch, "E105.MirrorCS", {"start": v(0, -90) * mm, "end": v(0, -120) * mm, "construction": true});
            skCircle(sketch, "E106.MirrorC", {"center": v(0, -120) * mm, "radius": 6 * mm});
            skLineSegment(sketch, "E107.MirrorCS", {"start": v(-15, -120) * mm, "end": v(-15, -108) * mm});
            skLineSegment(sketch, "E108.MirrorCS", {"start": v(-15, -108) * mm, "end": v(-33, -90) * mm});
            skSolve(sketch);
        }
        {
            var Q0;
            Q0 = qSketchRegion(id + "F16", true);
            var Q1;
            Q1=makeQuery(id+"F2.opExtrude","CAP_FACE",FACE,{"disambiguationData":[OSD([sQuery(id+"F0.wireOp",EDGE,"E12"),sQuery(id+"F0.wireOp",EDGE,"E13"),sQuery(id+"F0.wireOp",EDGE,"E14"),sQuery(id+"F0.wireOp",EDGE,"E15"),sQuery(id+"F0.wireOp",EDGE,"E17.filletArc"),sQuery(id+"F0.wireOp",EDGE,"E18.filletArc"),sQuery(id+"F0.wireOp",EDGE,"E19.filletArc"),sQuery(id+"F0.wireOp",EDGE,"E20.filletArc"),sQuery(id+"F0.wireOp",EDGE,"E25.0"),sQuery(id+"F0.wireOp",EDGE,"E25.1"),sQuery(id+"F0.wireOp",EDGE,"E25.2"),sQuery(id+"F0.wireOp",EDGE,"E25.3"),sQuery(id+"F0.wireOp",EDGE,"E25.4"),sQuery(id+"F0.wireOp",EDGE,"E25.5"),sQuery(id+"F0.wireOp",EDGE,"E25.6"),sQuery(id+"F0.wireOp",EDGE,"E25.7")])],"isStart":false});
            extrude(context, id + "F17", {"entities" : qUnion([Q0]), "endBound" : BoundingType.UP_TO_SURFACE, "depth" : 25 * mm, "endBoundEntityFace" : qUnion([Q1]), "offsetDistance" : 25 * mm});
        }
    });
